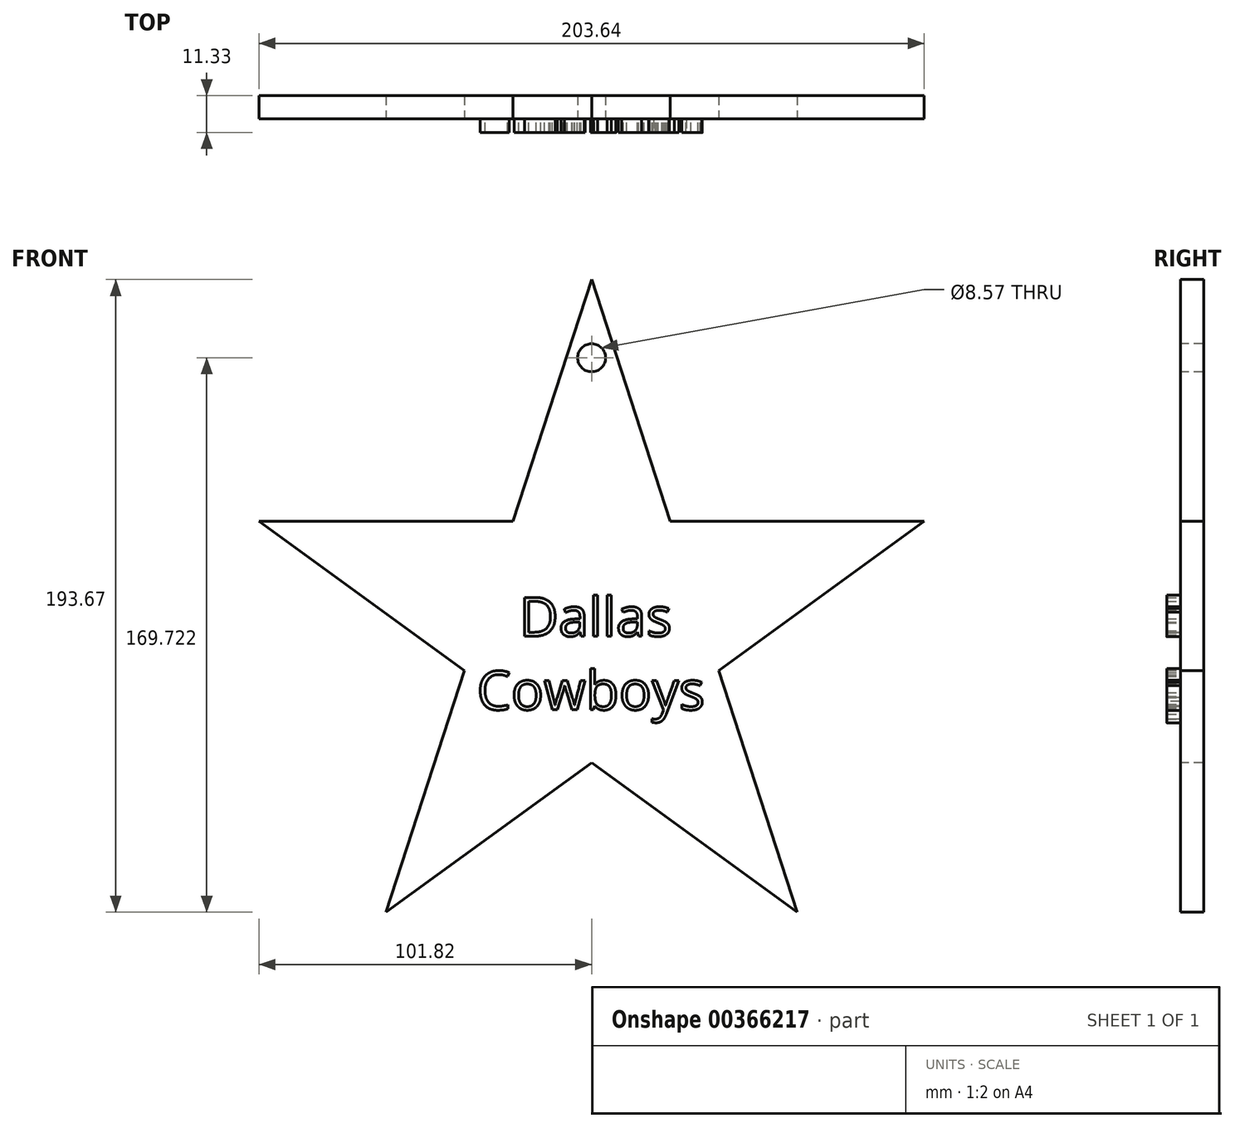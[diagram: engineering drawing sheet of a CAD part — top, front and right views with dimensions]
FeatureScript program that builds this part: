
annotation { "Feature Type Name" : "Feature", "Feature Type Description" : "" }
export const myFeature = defineFeature(function(context is Context, id is Id, definition is map)
    precondition{}
    {
        {
            var Q0;
            Q0=qCreatedBy(makeId("Front.planeOp"),FACE);
            var sketch = newSketch(context, id + "F0", { "sketchPlane" : qUnion([Q0])});
            skPoint(sketch, "E0.0.midPoint", {"position": v(19.45, -26.76) * mm});
            skLineSegment(sketch, "E1", {"start": v(0, -40.9) * mm, "end": v(-62.93, -86.61) * mm});
            skLineSegment(sketch, "E2", {"start": v(-62.93, -86.61) * mm, "end": v(-38.9, -12.64) * mm});
            skLineSegment(sketch, "E3", {"start": v(-38.9, -12.64) * mm, "end": v(-101.82, 33.08) * mm});
            skLineSegment(sketch, "E4", {"start": v(-101.82, 33.08) * mm, "end": v(-24.04, 33.08) * mm});
            skLineSegment(sketch, "E5", {"start": v(-24.04, 33.08) * mm, "end": v(0, 107.06) * mm});
            skLineSegment(sketch, "E6", {"start": v(0, 107.06) * mm, "end": v(24.04, 33.08) * mm});
            skLineSegment(sketch, "E7", {"start": v(24.04, 33.08) * mm, "end": v(101.82, 33.08) * mm});
            skLineSegment(sketch, "E8", {"start": v(101.82, 33.08) * mm, "end": v(38.9, -12.64) * mm});
            skLineSegment(sketch, "E9", {"start": v(38.9, -12.64) * mm, "end": v(62.93, -86.61) * mm});
            skLineSegment(sketch, "E10", {"start": v(62.93, -86.61) * mm, "end": v(0, -40.9) * mm});
            skLineSegment(sketch, "E11.0", {"start": v(-67.42, 21.9) * mm, "end": v(-15.92, 21.9) * mm});
            skLineSegment(sketch, "E11.1", {"start": v(-25.75, -8.37) * mm, "end": v(-67.42, 21.9) * mm});
            skLineSegment(sketch, "E11.2", {"start": v(-15.92, 21.9) * mm, "end": v(0, 70.9) * mm});
            skLineSegment(sketch, "E11.3", {"start": v(-41.67, -57.35) * mm, "end": v(-25.75, -8.37) * mm});
            skLineSegment(sketch, "E11.4", {"start": v(0, -27.08) * mm, "end": v(-41.67, -57.35) * mm});
            skLineSegment(sketch, "E11.5", {"start": v(41.67, -57.35) * mm, "end": v(0, -27.08) * mm});
            skLineSegment(sketch, "E11.6", {"start": v(0, 70.9) * mm, "end": v(15.92, 21.9) * mm});
            skLineSegment(sketch, "E11.7", {"start": v(15.92, 21.9) * mm, "end": v(67.42, 21.9) * mm});
            skLineSegment(sketch, "E11.8", {"start": v(67.42, 21.9) * mm, "end": v(25.75, -8.37) * mm});
            skLineSegment(sketch, "E11.9", {"start": v(25.75, -8.37) * mm, "end": v(41.67, -57.35) * mm});
            skCircle(sketch, "E12", {"center": v(0, 83.11) * mm, "radius": 4.28 * mm});
            skSolve(sketch);
        }
        {
            var Q0;
            Q0=makeQuery(id+"F0.imprint","IMPRINT",FACE,{"disambiguationData":[TD([[makeQuery(id+"F0.imprint","IMPRINT",EDGE,{"derivedFrom":sQuery(id+"F0.wireOp",EDGE,"E1")}),-1.0]])]});
            var Q1;
            Q1=makeQuery(id+"F0.imprint","IMPRINT",FACE,{"disambiguationData":[TD([[makeQuery(id+"F0.imprint","IMPRINT",EDGE,{"derivedFrom":sQuery(id+"F0.wireOp",EDGE,"E11.0")}),-1.0]])]});
            var Q2;
            {var subQ0=sQuery(id+"F0.wireOp",EDGE,"E6");var subQ1=sQuery(id+"F0.wireOp",EDGE,"E5");var subQ2=makeQuery(id+"F0.imprint","INTERSECT",VERTEX,{"derivedFrom":[subQ1,subQ0]});Q2=makeQuery(id+"F0.imprint","IMPRINT",FACE,{"disambiguationData":[TD([[makeQuery(id+"F0.imprint","IMPRINT",EDGE,{"disambiguationData":[TD([[subQ2,1.0]])],"derivedFrom":subQ1}),-1.0]])]});}
            extrude(context, id + "F1", {"entities" : qUnion([Q0, Q1, Q2]), "oppositeDirection" : true, "depth" : 7.11 * mm});
        }
        {
            var Q0;
            Q0=makeQuery(id+"F1.opExtrude","CAP_FACE",FACE,{"disambiguationData":[OSD([sQuery(id+"F0.wireOp",EDGE,"E1"),sQuery(id+"F0.wireOp",EDGE,"E2"),sQuery(id+"F0.wireOp",EDGE,"E3"),sQuery(id+"F0.wireOp",EDGE,"E4"),sQuery(id+"F0.wireOp",EDGE,"E5"),sQuery(id+"F0.wireOp",EDGE,"E6"),sQuery(id+"F0.wireOp",EDGE,"E7"),sQuery(id+"F0.wireOp",EDGE,"E8"),sQuery(id+"F0.wireOp",EDGE,"E9"),sQuery(id+"F0.wireOp",EDGE,"E10"),sQuery(id+"F0.wireOp",EDGE,"EGw3xsbS-JmS8-ogfa-NjG7-HKWAKOLkqYKy")])],"isStart":true});
            var sketch = newSketch(context, id + "F2", { "sketchPlane" : qUnion([Q0])});
            skText(sketch, "E13", { "text": "   Dallas \nCowboys", "fontName": "OpenSans-Regular.ttf"});
            const initialGuessF2  = {"E13": [-0.03512, -0.00209, 1, 0, 0.01193]};
            skSetInitialGuess(sketch, initialGuessF2);
            skSolve(sketch);
        }
        {
            var Q0;
            Q0=makeQuery(id+"F2.imprint","IMPRINT",FACE,{"disambiguationData":[TD([[makeQuery(id+"F2.imprint","IMPRINT",EDGE,{"derivedFrom":sQuery(id+"F2.wireOp",EDGE,"E13.sketch_text.stroke-0")}),-1.0]])]});
            var Q1;
            Q1=makeQuery(id+"F2.imprint","IMPRINT",FACE,{"disambiguationData":[TD([[makeQuery(id+"F2.imprint","IMPRINT",EDGE,{"derivedFrom":sQuery(id+"F2.wireOp",EDGE,"E13.sketch_text.stroke-14")}),-1.0]])]});
            var Q2;
            Q2=makeQuery(id+"F2.imprint","IMPRINT",FACE,{"disambiguationData":[TD([[makeQuery(id+"F2.imprint","IMPRINT",EDGE,{"derivedFrom":sQuery(id+"F2.wireOp",EDGE,"E13.sketch_text.stroke-41")}),-1.0]])]});
            var Q3;
            Q3=makeQuery(id+"F2.imprint","IMPRINT",FACE,{"disambiguationData":[TD([[makeQuery(id+"F2.imprint","IMPRINT",EDGE,{"derivedFrom":sQuery(id+"F2.wireOp",EDGE,"E13.sketch_text.stroke-45")}),-1.0]])]});
            var Q4;
            Q4=makeQuery(id+"F2.imprint","IMPRINT",FACE,{"disambiguationData":[TD([[makeQuery(id+"F2.imprint","IMPRINT",EDGE,{"derivedFrom":sQuery(id+"F2.wireOp",EDGE,"E13.sketch_text.stroke-49")}),-1.0]])]});
            var Q5;
            Q5=makeQuery(id+"F2.imprint","IMPRINT",FACE,{"disambiguationData":[TD([[makeQuery(id+"F2.imprint","IMPRINT",EDGE,{"derivedFrom":sQuery(id+"F2.wireOp",EDGE,"E13.sketch_text.stroke-76")}),-1.0]])]});
            var Q6;
            Q6=makeQuery(id+"F2.imprint","IMPRINT",FACE,{"disambiguationData":[TD([[makeQuery(id+"F2.imprint","IMPRINT",EDGE,{"derivedFrom":sQuery(id+"F2.wireOp",EDGE,"E13.sketch_text.stroke-101")}),-1.0]])]});
            var Q7;
            Q7=makeQuery(id+"F2.imprint","IMPRINT",FACE,{"disambiguationData":[TD([[makeQuery(id+"F2.imprint","IMPRINT",EDGE,{"derivedFrom":sQuery(id+"F2.wireOp",EDGE,"E13.sketch_text.stroke-116")}),-1.0]])]});
            var Q8;
            Q8=makeQuery(id+"F2.imprint","IMPRINT",FACE,{"disambiguationData":[TD([[makeQuery(id+"F2.imprint","IMPRINT",EDGE,{"derivedFrom":sQuery(id+"F2.wireOp",EDGE,"E13.sketch_text.stroke-133")}),-1.0]])]});
            var Q9;
            Q9=makeQuery(id+"F2.imprint","IMPRINT",FACE,{"disambiguationData":[TD([[makeQuery(id+"F2.imprint","IMPRINT",EDGE,{"derivedFrom":sQuery(id+"F2.wireOp",EDGE,"E13.sketch_text.stroke-156")}),-1.0]])]});
            var Q10;
            Q10=makeQuery(id+"F2.imprint","IMPRINT",FACE,{"disambiguationData":[TD([[makeQuery(id+"F2.imprint","IMPRINT",EDGE,{"derivedFrom":sQuery(id+"F2.wireOp",EDGE,"E13.sketch_text.stroke-179")}),-1.0]])]});
            var Q11;
            Q11=makeQuery(id+"F2.imprint","IMPRINT",FACE,{"disambiguationData":[TD([[makeQuery(id+"F2.imprint","IMPRINT",EDGE,{"derivedFrom":sQuery(id+"F2.wireOp",EDGE,"E13.sketch_text.stroke-196")}),-1.0]])]});
            var Q12;
            Q12=makeQuery(id+"F2.imprint","IMPRINT",FACE,{"disambiguationData":[TD([[makeQuery(id+"F2.imprint","IMPRINT",EDGE,{"derivedFrom":sQuery(id+"F2.wireOp",EDGE,"E13.sketch_text.stroke-212")}),-1.0]])]});
            extrude(context, id + "F3", {"entities" : qUnion([Q0, Q1, Q2, Q3, Q4, Q5, Q6, Q7, Q8, Q9, Q10, Q11, Q12]), "operationType" : NewBodyOperationType.ADD, "depth" : 4.22 * mm});
        }
    });
